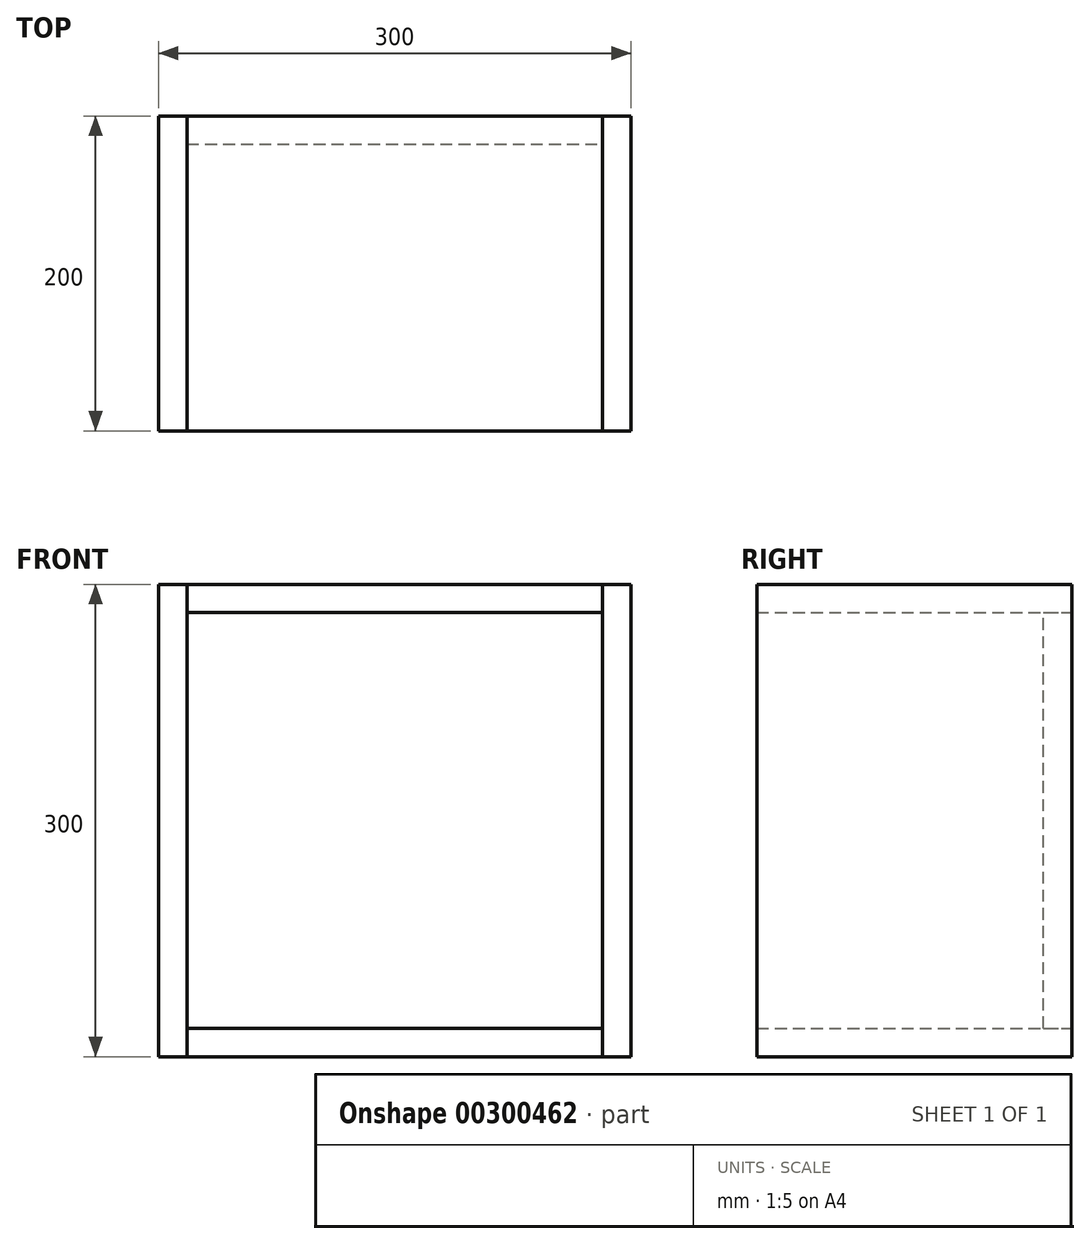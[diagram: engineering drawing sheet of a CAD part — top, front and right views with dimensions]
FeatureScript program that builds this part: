
annotation { "Feature Type Name" : "Feature", "Feature Type Description" : "" }
export const myFeature = defineFeature(function(context is Context, id is Id, definition is map)
    precondition{}
    {
        {
            assignVariable(context, id + "F0", {"name" : "t", "anyValue" : 200});
        }
        {
            var Q0;
            Q0=qCreatedBy(makeId("Front.planeOp"),FACE);
            var sketch = newSketch(context, id + "F1", { "sketchPlane" : qUnion([Q0])});
            skLineSegment(sketch, "E0.bottom", {"start": v(0, 0) * mm, "end": v(300, 0) * mm});
            skLineSegment(sketch, "E0.top", {"start": v(0, 300) * mm, "end": v(300, 300) * mm});
            skLineSegment(sketch, "E0.left", {"start": v(0, 0) * mm, "end": v(0, 300) * mm});
            skLineSegment(sketch, "E0.right", {"start": v(300, 0) * mm, "end": v(300, 300) * mm});
            skLineSegment(sketch, "E1.0", {"start": v(18, 282) * mm, "end": v(282, 282) * mm});
            skLineSegment(sketch, "E1.1", {"start": v(18, 18) * mm, "end": v(18, 282) * mm});
            skLineSegment(sketch, "E1.2", {"start": v(18, 18) * mm, "end": v(282, 18) * mm});
            skLineSegment(sketch, "E1.3", {"start": v(282, 18) * mm, "end": v(282, 282) * mm});
            skLineSegment(sketch, "E2", {"start": v(18, 282) * mm, "end": v(18, 300) * mm});
            skLineSegment(sketch, "E3", {"start": v(18, 18) * mm, "end": v(18, 0) * mm});
            skLineSegment(sketch, "E4", {"start": v(282, 282) * mm, "end": v(282, 300) * mm});
            skLineSegment(sketch, "E5", {"start": v(282, 18) * mm, "end": v(282, 0) * mm});
            skSolve(sketch);
        }
        {
            var Q0;
            Q0=makeQuery(id+"F1.imprint","IMPRINT",FACE,{"disambiguationData":[TD([[makeQuery(id+"F1.imprint","IMPRINT",EDGE,{"derivedFrom":sQuery(id+"F1.wireOp",EDGE,"E1.0")}),1.0]])]});
            var Q1;
            Q1=makeQuery(id+"F1.imprint","IMPRINT",FACE,{"disambiguationData":[TD([[makeQuery(id+"F1.imprint","IMPRINT",EDGE,{"derivedFrom":sQuery(id+"F1.wireOp",EDGE,"E1.2")}),-1.0]])]});
            extrude(context, id + "F2", {"entities" : qUnion([Q0, Q1]), "depth" : (getVariable(context, 't')) * mm});
        }
        {
            var Q0;
            {var subQ0=sQuery(id+"F1.wireOp",EDGE,"E0.left");Q0=makeQuery(id+"F1.imprint","IMPRINT",FACE,{"disambiguationData":[TD([[makeQuery(id+"F1.imprint","IMPRINT",EDGE,{"derivedFrom":subQ0}),-1.0]])]});}
            var Q1;
            {var subQ0=sQuery(id+"F1.wireOp",EDGE,"E0.right");Q1=makeQuery(id+"F1.imprint","IMPRINT",FACE,{"disambiguationData":[TD([[makeQuery(id+"F1.imprint","IMPRINT",EDGE,{"derivedFrom":subQ0}),1.0]])]});}
            extrude(context, id + "F3", {"entities" : qUnion([Q0, Q1]), "depth" : (getVariable(context, 't')) * mm});
        }
        {
            var Q0;
            Q0=makeQuery(id+"F1.imprint","IMPRINT",FACE,{"disambiguationData":[TD([[makeQuery(id+"F1.imprint","IMPRINT",EDGE,{"derivedFrom":sQuery(id+"F1.wireOp",EDGE,"E1.0")}),-1.0]])]});
            extrude(context, id + "F4", {"entities" : qUnion([Q0]), "depth" : 18 * mm});
        }
    });
